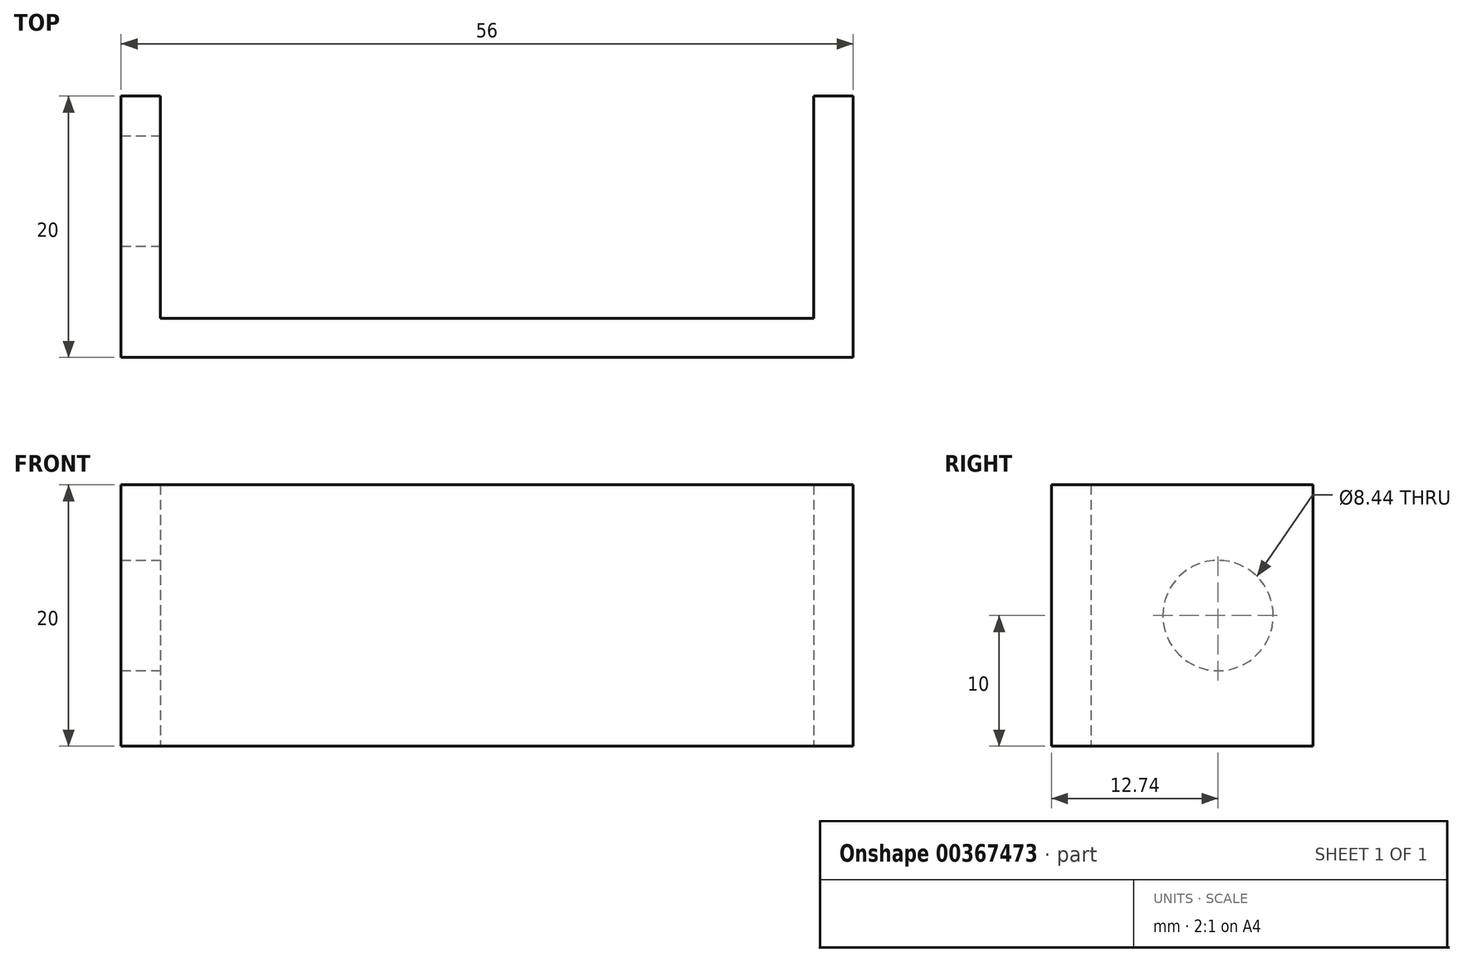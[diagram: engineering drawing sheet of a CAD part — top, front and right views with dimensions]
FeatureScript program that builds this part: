
annotation { "Feature Type Name" : "Feature", "Feature Type Description" : "" }
export const myFeature = defineFeature(function(context is Context, id is Id, definition is map)
    precondition{}
    {
        {
            var Q0;
            Q0=qCreatedBy(makeId("Top.planeOp"),FACE);
            var sketch = newSketch(context, id + "F0", { "sketchPlane" : qUnion([Q0])});
            skLineSegment(sketch, "E0.bottom", {"start": v(0, 0) * mm, "end": v(50, 0) * mm});
            skLineSegment(sketch, "E0.top", {"start": v(0, -3) * mm, "end": v(50, -3) * mm});
            skLineSegment(sketch, "E0.left", {"start": v(0, 0) * mm, "end": v(0, -3) * mm});
            skLineSegment(sketch, "E0.right", {"start": v(50, 0) * mm, "end": v(50, -3) * mm});
            skLineSegment(sketch, "E1.bottom", {"start": v(0, -3) * mm, "end": v(-3, -3) * mm});
            skLineSegment(sketch, "E1.top", {"start": v(0, 17) * mm, "end": v(-3, 17) * mm});
            skLineSegment(sketch, "E1.left", {"start": v(0, -3) * mm, "end": v(0, 17) * mm});
            skLineSegment(sketch, "E1.right", {"start": v(-3, -3) * mm, "end": v(-3, 17) * mm});
            skLineSegment(sketch, "E2.bottom", {"start": v(50, -3) * mm, "end": v(53, -3) * mm});
            skLineSegment(sketch, "E2.top", {"start": v(50, 17) * mm, "end": v(53, 17) * mm});
            skLineSegment(sketch, "E2.left", {"start": v(50, -3) * mm, "end": v(50, 17) * mm});
            skLineSegment(sketch, "E2.right", {"start": v(53, -3) * mm, "end": v(53, 17) * mm});
            skSolve(sketch);
        }
        {
            var Q0;
            {var subQ3=sQuery(id+"F0.wireOp",EDGE,"E1.bottom");Q0=makeQuery(id+"F0.imprint","IMPRINT",FACE,{"disambiguationData":[TD([[makeQuery(id+"F0.imprint","IMPRINT",EDGE,{"derivedFrom":subQ3}),-1.0]])]});}
            var Q1;
            {var subQ3=sQuery(id+"F0.wireOp",EDGE,"E2.bottom");Q1=makeQuery(id+"F0.imprint","IMPRINT",FACE,{"disambiguationData":[TD([[makeQuery(id+"F0.imprint","IMPRINT",EDGE,{"derivedFrom":subQ3}),1.0]])]});}
            var Q2;
            {var subQ0=sQuery(id+"F0.wireOp",EDGE,"E0.bottom");Q2=makeQuery(id+"F0.imprint","IMPRINT",FACE,{"disambiguationData":[TD([[makeQuery(id+"F0.imprint","IMPRINT",EDGE,{"derivedFrom":subQ0}),-1.0]])]});}
            extrude(context, id + "F1", {"entities" : qUnion([Q0, Q1, Q2]), "depth" : 20 * mm});
        }
        {
            var Q0;
            Q0=makeQuery(id+"F1.opExtrude","SWEPT_FACE",FACE,{"disambiguationData":[OSD([sQuery(id+"F0.wireOp",EDGE,"E2.left")])]});
            var sketch = newSketch(context, id + "F2", { "sketchPlane" : qUnion([Q0])});
            skCircle(sketch, "E3", {"center": v(-9.74, 10) * mm, "radius": 4.22 * mm});
            skPoint(sketch, "E3.centerSnap0", {"position": v(-17, 10) * mm});
            skSolve(sketch);
        }
        {
            var Q0;
            Q0 = qSketchRegion(id + "F2", true);
            extrude(context, id + "F3", {"entities" : qUnion([Q0]), "operationType" : NewBodyOperationType.REMOVE, "depth" : 98.7 * mm});
        }
    });
